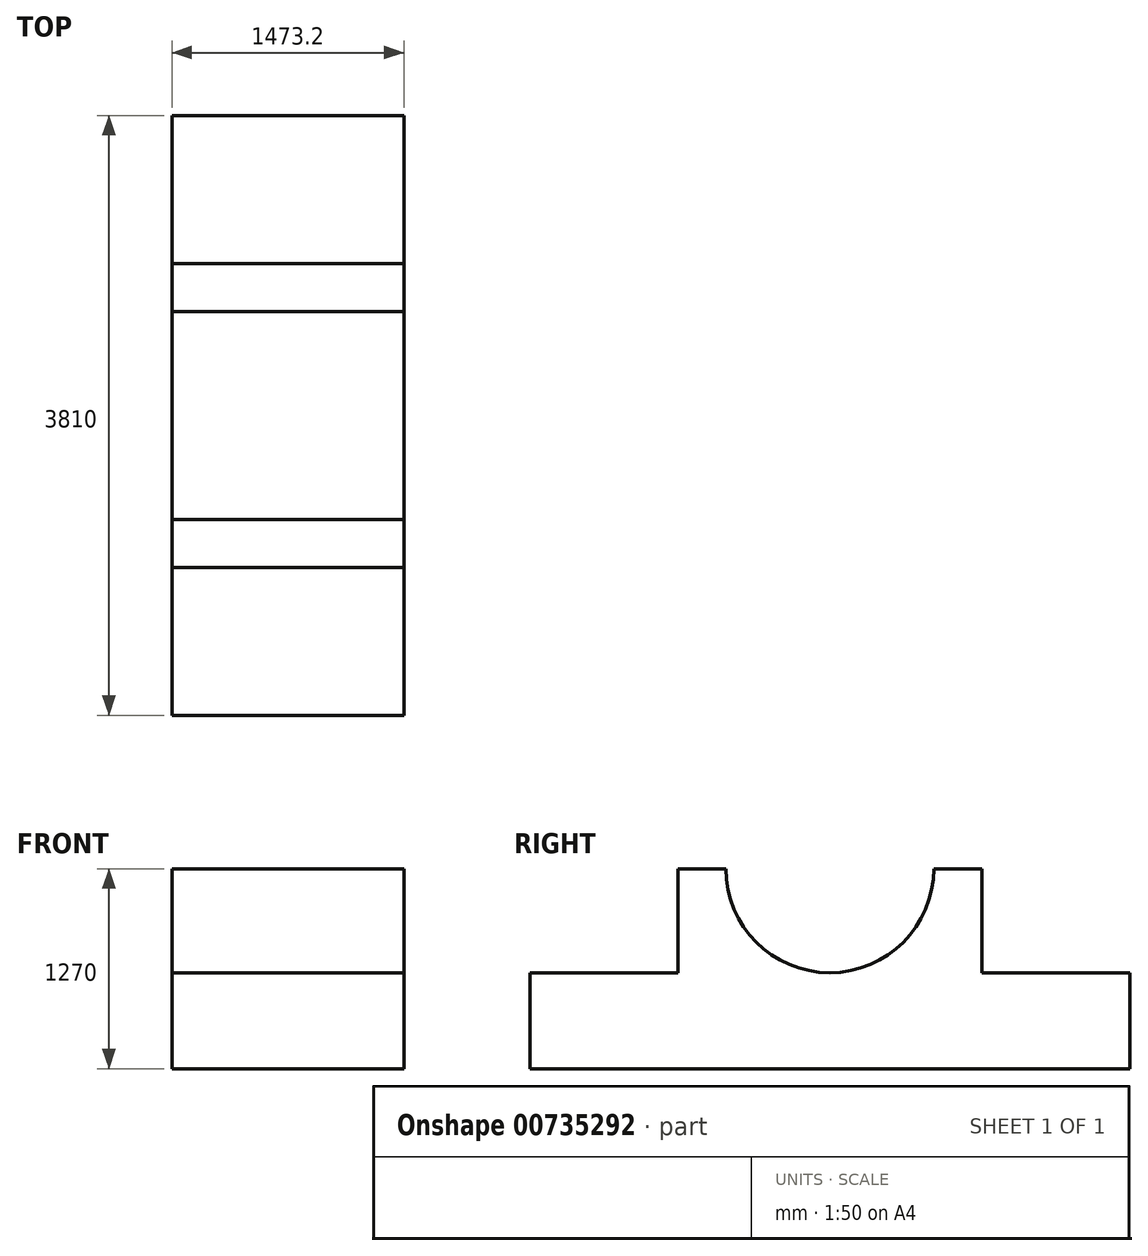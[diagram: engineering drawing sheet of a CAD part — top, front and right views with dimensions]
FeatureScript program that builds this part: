
annotation { "Feature Type Name" : "Feature", "Feature Type Description" : "" }
export const myFeature = defineFeature(function(context is Context, id is Id, definition is map)
    precondition{}
    {
        {
            var Q0;
            Q0=qCreatedBy(makeId("Right.planeOp"),FACE);
            var sketch = newSketch(context, id + "F0", { "sketchPlane" : qUnion([Q0])});
            skLineSegment(sketch, "E0", {"start": v(-76.87, -21.75) * mm, "end": v(3733.13, -21.75) * mm});
            skLineSegment(sketch, "E1", {"start": v(-76.87, -21.75) * mm, "end": v(-76.87, 587.85) * mm});
            skLineSegment(sketch, "E2", {"start": v(3733.13, -21.75) * mm, "end": v(3733.13, 587.85) * mm});
            skLineSegment(sketch, "E3", {"start": v(-76.87, 587.85) * mm, "end": v(862.93, 587.85) * mm});
            skLineSegment(sketch, "E4", {"start": v(3733.13, 587.85) * mm, "end": v(2793.33, 587.85) * mm});
            skLineSegment(sketch, "E5", {"start": v(862.93, 587.85) * mm, "end": v(862.93, 1248.25) * mm});
            skLineSegment(sketch, "E6", {"start": v(2793.33, 587.85) * mm, "end": v(2793.33, 1248.25) * mm});
            skLineSegment(sketch, "E7", {"start": v(862.93, 1248.25) * mm, "end": v(1167.73, 1248.25) * mm});
            skLineSegment(sketch, "E8", {"start": v(1167.73, 1248.25) * mm, "end": v(1828.13, 1248.25) * mm});
            skLineSegment(sketch, "E9", {"start": v(2793.33, 1248.25) * mm, "end": v(2488.53, 1248.25) * mm});
            skCircle(sketch, "E10", {"center": v(1828.13, 1248.25) * mm, "radius": 660.4 * mm});
            skSolve(sketch);
        }
        {
            var Q0;
            Q0=makeQuery(id+"F0.imprint","IMPRINT",FACE,{"disambiguationData":[TD([[makeQuery(id+"F0.imprint","IMPRINT",EDGE,{"derivedFrom":sQuery(id+"F0.wireOp",EDGE,"E0")}),1.0]])]});
            extrude(context, id + "F1", {"entities" : qUnion([Q0]), "depth" : 1473.2 * mm, "offsetDistance" : 25.4 * mm});
        }
    });
